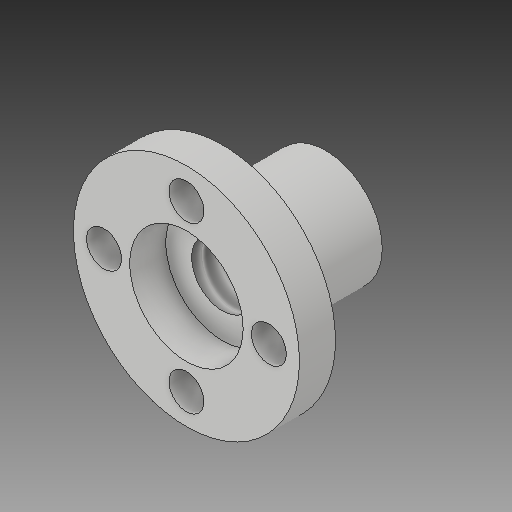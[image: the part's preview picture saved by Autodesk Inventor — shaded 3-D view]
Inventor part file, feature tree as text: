
AUTODESK INVENTOR PART (.ipt)
format: ipt  version: 2017 (Build 210142000, 142)  size: 138,240 bytes
history: native  units: mm
features: other x3, sketch x3
ambient origin geometry x8: Origin, YZ Plane, XZ Plane, XY Plane, X Axis, Y Axis, Z Axis, Center Point
bodies: Solid1 (feature_tree)
feature tree (6):
  other  "Brass-Nut.ipt"
  other  "Solid1::Brass-Nut.ipt"
  other  "TaggingFeature1"
  sketch  "Sketch1"  dims[d0=10.0mm]
  sketch  "Sketch2"
  sketch  "Sketch3"
